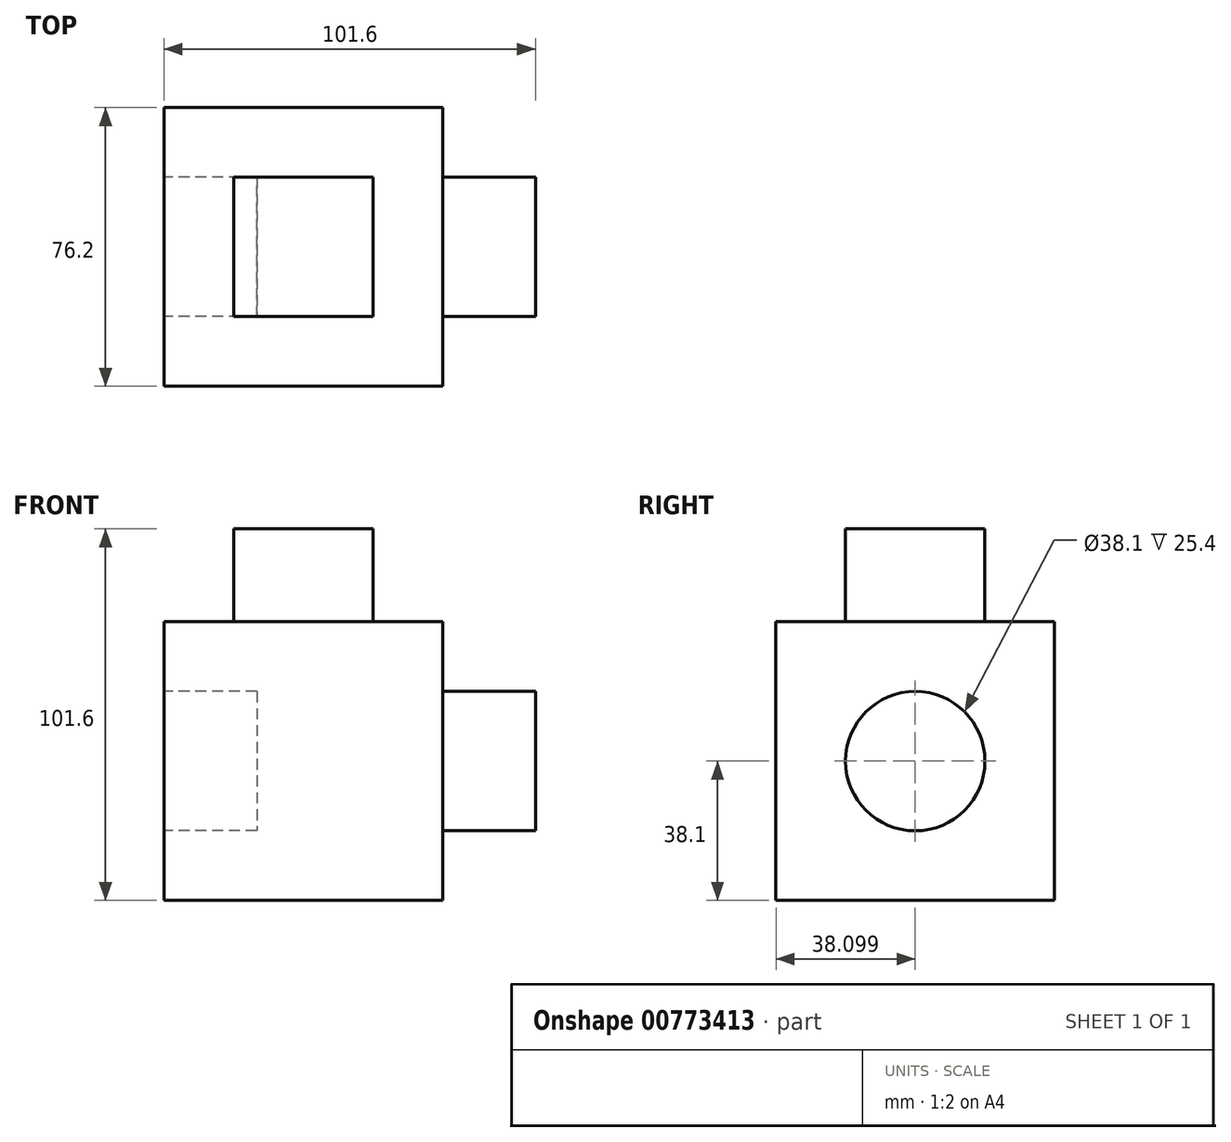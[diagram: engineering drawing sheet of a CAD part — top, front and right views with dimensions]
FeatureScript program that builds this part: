
annotation { "Feature Type Name" : "Feature", "Feature Type Description" : "" }
export const myFeature = defineFeature(function(context is Context, id is Id, definition is map)
    precondition{}
    {
        {
            var Q0;
            Q0=qCreatedBy(makeId("Top.planeOp"),FACE);
            var sketch = newSketch(context, id + "F0", { "sketchPlane" : qUnion([Q0])});
            skLineSegment(sketch, "E0.bottom", {"start": v(-67.81, -50.06) * mm, "end": v(8.39, -50.06) * mm});
            skLineSegment(sketch, "E0.top", {"start": v(-67.81, 26.14) * mm, "end": v(8.39, 26.14) * mm});
            skLineSegment(sketch, "E0.left", {"start": v(-67.81, -50.06) * mm, "end": v(-67.81, 26.14) * mm});
            skLineSegment(sketch, "E0.right", {"start": v(8.39, -50.06) * mm, "end": v(8.39, 26.14) * mm});
            skSolve(sketch);
        }
        {
            var Q0;
            Q0=makeQuery(id+"F0.imprint","IMPRINT",FACE,{"disambiguationData":[TD([[makeQuery(id+"F0.imprint","IMPRINT",EDGE,{"derivedFrom":sQuery(id+"F0.wireOp",EDGE,"E0.bottom")}),1.0]])]});
            extrude(context, id + "F1", {"entities" : qUnion([Q0]), "depth" : 76.2 * mm, "offsetDistance" : 25.4 * mm});
        }
        {
            var Q0;
            Q0=makeQuery(id+"F1.opExtrude","CAP_FACE",FACE,{"disambiguationData":[OSD([sQuery(id+"F0.wireOp",EDGE,"E0.bottom"),sQuery(id+"F0.wireOp",EDGE,"E0.top"),sQuery(id+"F0.wireOp",EDGE,"E0.left"),sQuery(id+"F0.wireOp",EDGE,"E0.right")])],"isStart":false});
            var sketch = newSketch(context, id + "F2", { "sketchPlane" : qUnion([Q0])});
            skLineSegment(sketch, "E1.bottom", {"start": v(-10.66, 7.09) * mm, "end": v(-48.76, 7.09) * mm});
            skLineSegment(sketch, "E1.top", {"start": v(-10.66, -31.01) * mm, "end": v(-48.76, -31.01) * mm});
            skLineSegment(sketch, "E1.left", {"start": v(-10.66, 7.09) * mm, "end": v(-10.66, -31.01) * mm});
            skLineSegment(sketch, "E1.right", {"start": v(-48.76, 7.09) * mm, "end": v(-48.76, -31.01) * mm});
            skSolve(sketch);
        }
        {
            var Q0;
            Q0=makeQuery(id+"F1.opExtrude","SWEPT_FACE",FACE,{"disambiguationData":[OSD([sQuery(id+"F0.wireOp",EDGE,"E0.right")])]});
            var sketch = newSketch(context, id + "F3", { "sketchPlane" : qUnion([Q0])});
            skCircle(sketch, "E2", {"center": v(-11.96, 38.1) * mm, "radius": 19.05 * mm});
            skSolve(sketch);
        }
        {
            var Q0;
            Q0=makeQuery(id+"F1.opExtrude","SWEPT_FACE",FACE,{"disambiguationData":[OSD([sQuery(id+"F0.wireOp",EDGE,"E0.left")])]});
            var sketch = newSketch(context, id + "F4", { "sketchPlane" : qUnion([Q0])});
            skCircle(sketch, "E3", {"center": v(11.96, 38.1) * mm, "radius": 19.05 * mm});
            skSolve(sketch);
        }
        {
            var Q0;
            Q0=makeQuery(id+"F2.imprint","IMPRINT",FACE,{"disambiguationData":[TD([[makeQuery(id+"F2.imprint","IMPRINT",EDGE,{"derivedFrom":sQuery(id+"F2.wireOp",EDGE,"E1.bottom")}),1.0]])]});
            extrude(context, id + "F5", {"entities" : qUnion([Q0]), "operationType" : NewBodyOperationType.ADD, "depth" : 25.4 * mm, "offsetDistance" : 25.4 * mm});
        }
        {
            var Q0;
            Q0=makeQuery(id+"F3.imprint","IMPRINT",FACE,{"disambiguationData":[TD([[makeQuery(id+"F3.imprint","IMPRINT",EDGE,{"derivedFrom":sQuery(id+"F3.wireOp",EDGE,"E2")}),1.0]])]});
            extrude(context, id + "F6", {"entities" : qUnion([Q0]), "operationType" : NewBodyOperationType.ADD, "depth" : 25.4 * mm, "offsetDistance" : 25.4 * mm});
        }
        {
            var Q0;
            Q0=makeQuery(id+"F4.imprint","IMPRINT",FACE,{"disambiguationData":[TD([[makeQuery(id+"F4.imprint","IMPRINT",EDGE,{"derivedFrom":sQuery(id+"F4.wireOp",EDGE,"E3")}),1.0]])]});
            extrude(context, id + "F7", {"entities" : qUnion([Q0]), "operationType" : NewBodyOperationType.REMOVE, "oppositeDirection" : true, "depth" : 25.4 * mm, "offsetDistance" : 25.4 * mm});
        }
    });
